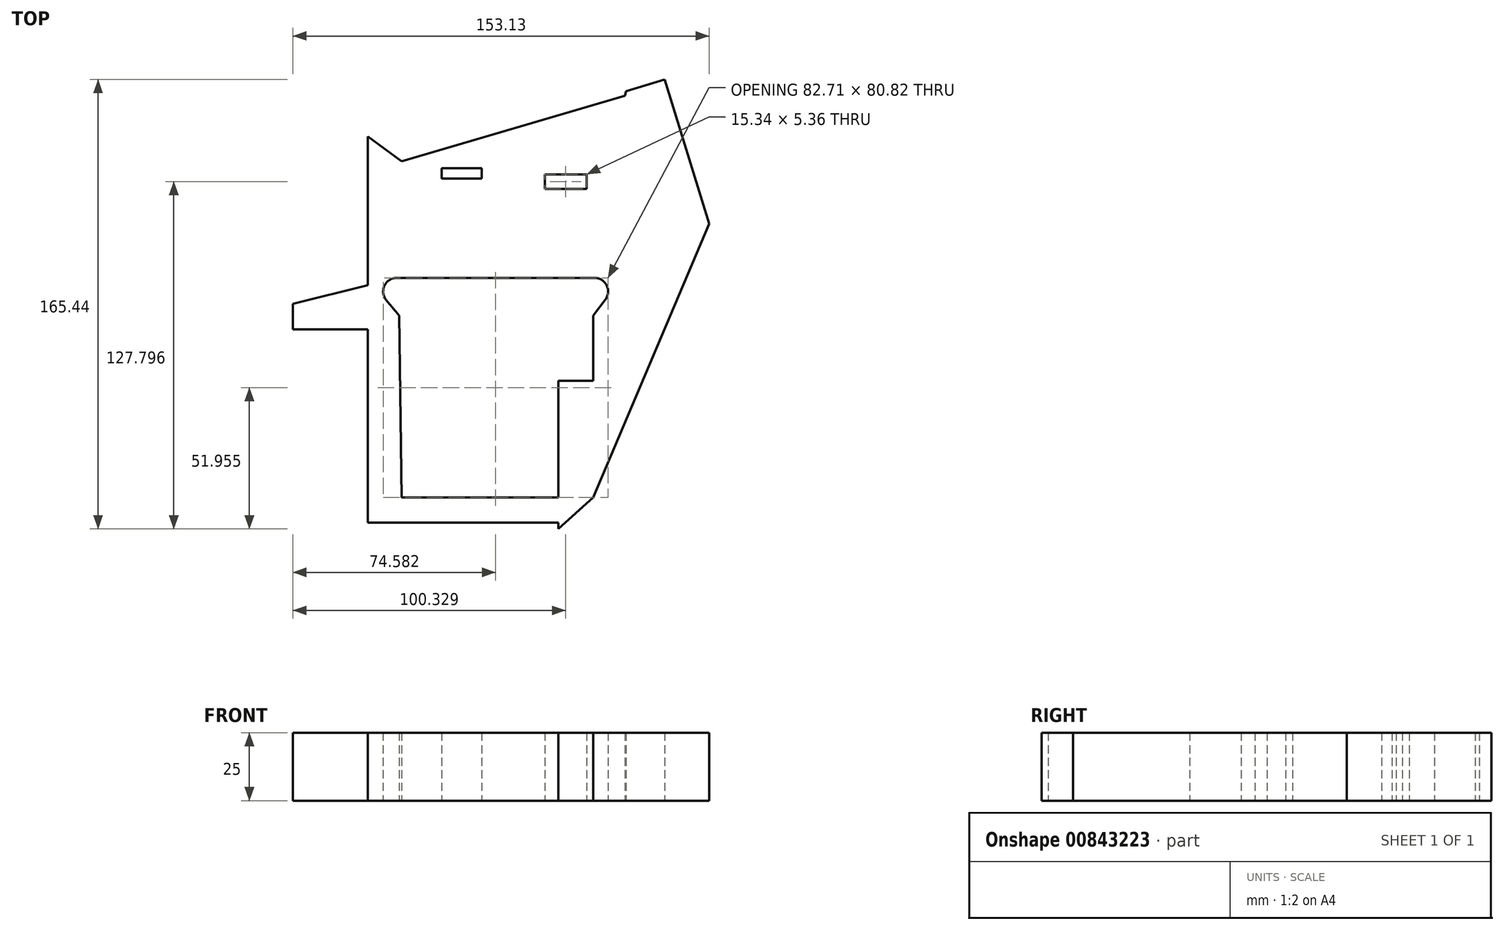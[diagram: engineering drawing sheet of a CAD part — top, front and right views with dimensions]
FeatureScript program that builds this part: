
annotation { "Feature Type Name" : "Feature", "Feature Type Description" : "" }
export const myFeature = defineFeature(function(context is Context, id is Id, definition is map)
    precondition{}
    {
        {
            var Q0;
            Q0=qCreatedBy(makeId("Top.planeOp"),FACE);
            var sketch = newSketch(context, id + "F0", { "sketchPlane" : qUnion([Q0])});
            skLineSegment(sketch, "E0", {"start": v(-30.35, 30.64) * mm, "end": v(41, 30.64) * mm});
            skLineSegment(sketch, "E1", {"start": v(41, 30.64) * mm, "end": v(41, -36.27) * mm});
            skLineSegment(sketch, "E2", {"start": v(41, -36.27) * mm, "end": v(-29.46, -36.27) * mm});
            skLineSegment(sketch, "E3", {"start": v(-29.46, -36.27) * mm, "end": v(-30.35, 30.64) * mm});
            skLineSegment(sketch, "E4", {"start": v(-30.35, 30.64) * mm, "end": v(-35.1, 36.36) * mm});
            skLineSegment(sketch, "E5", {"start": v(-31.25, 44.56) * mm, "end": v(41.53, 44.56) * mm});
            skLineSegment(sketch, "E6", {"start": v(45.5, 36.52) * mm, "end": v(41, 30.64) * mm});
            skPoint(sketch, "E7.visualSharp", {"position": v(-41.9, 44.56) * mm});
            skArc(sketch, "E7.filletArc", {"start": v(-31.25, 44.56) * mm, "mid": v(-35.77, 41.68) * mm, "end": v(-35.1, 36.36) * mm});
            skPoint(sketch, "E8.visualSharp", {"position": v(51.66, 44.56) * mm});
            skArc(sketch, "E8.filletArc", {"start": v(45.5, 36.52) * mm, "mid": v(46.02, 41.77) * mm, "end": v(41.53, 44.56) * mm});
            skLineSegment(sketch, "E9", {"start": v(-30.35, 30.64) * mm, "end": v(-41.9, 25.6) * mm});
            skLineSegment(sketch, "E10", {"start": v(-41.9, 25.6) * mm, "end": v(-41.9, -45.44) * mm});
            skLineSegment(sketch, "E11", {"start": v(-41.9, -45.44) * mm, "end": v(-29.46, -36.27) * mm});
            skLineSegment(sketch, "E12", {"start": v(41, 30.64) * mm, "end": v(28.27, 25.6) * mm});
            skLineSegment(sketch, "E13", {"start": v(28.27, 25.6) * mm, "end": v(28.27, -47.81) * mm});
            skLineSegment(sketch, "E14", {"start": v(28.27, -47.81) * mm, "end": v(41, -36.27) * mm});
            skLineSegment(sketch, "E15", {"start": v(-41.9, -45.44) * mm, "end": v(28.27, -45.44) * mm});
            skLineSegment(sketch, "E16", {"start": v(-41.9, 25.6) * mm, "end": v(28.27, 25.6) * mm});
            skLineSegment(sketch, "E17.bottom", {"start": v(5.18, -6.07) * mm, "end": v(23.24, -6.07) * mm});
            skLineSegment(sketch, "E17.top", {"start": v(5.18, -13.47) * mm, "end": v(23.24, -13.47) * mm});
            skLineSegment(sketch, "E17.left", {"start": v(5.18, -6.07) * mm, "end": v(5.18, -13.47) * mm});
            skLineSegment(sketch, "E17.right", {"start": v(23.24, -6.07) * mm, "end": v(23.24, -13.47) * mm});
            skLineSegment(sketch, "E18.bottom", {"start": v(-22.65, -6.07) * mm, "end": v(-6.96, -6.07) * mm});
            skLineSegment(sketch, "E18.top", {"start": v(-22.65, -13.47) * mm, "end": v(-6.96, -13.47) * mm});
            skLineSegment(sketch, "E18.left", {"start": v(-22.65, -6.07) * mm, "end": v(-22.65, -13.47) * mm});
            skLineSegment(sketch, "E18.right", {"start": v(-6.96, -6.07) * mm, "end": v(-6.96, -13.47) * mm});
            skLineSegment(sketch, "E19", {"start": v(-17.91, -13.47) * mm, "end": v(-17.91, -6.07) * mm});
            skLineSegment(sketch, "E20", {"start": v(-11.7, -13.47) * mm, "end": v(-11.7, -6.07) * mm});
            skLineSegment(sketch, "E21", {"start": v(11.4, -13.47) * mm, "end": v(11.4, -6.07) * mm});
            skLineSegment(sketch, "E22", {"start": v(17.02, -13.47) * mm, "end": v(17.02, -6.07) * mm});
            skLineSegment(sketch, "E23", {"start": v(-6.07, 3.7) * mm, "end": v(-5.59, -32.43) * mm});
            skLineSegment(sketch, "E24", {"start": v(-5.59, -32.43) * mm, "end": v(3.1, -32.32) * mm});
            skLineSegment(sketch, "E25", {"start": v(3.1, -32.32) * mm, "end": v(3.1, 3.7) * mm});
            skLineSegment(sketch, "E26", {"start": v(3.1, 3.7) * mm, "end": v(-6.07, 3.7) * mm});
            skLineSegment(sketch, "E27", {"start": v(8.44, 15.84) * mm, "end": v(23.24, 15.84) * mm});
            skLineSegment(sketch, "E28", {"start": v(23.24, 15.84) * mm, "end": v(23.24, 7.55) * mm});
            skLineSegment(sketch, "E29", {"start": v(23.24, 7.55) * mm, "end": v(9.62, 7.55) * mm});
            skLineSegment(sketch, "E30", {"start": v(9.62, 7.55) * mm, "end": v(9.62, 15.84) * mm});
            skLineSegment(sketch, "E31.bottom", {"start": v(-22.35, 17.02) * mm, "end": v(-8.44, 17.02) * mm});
            skLineSegment(sketch, "E31.top", {"start": v(-22.35, 9.03) * mm, "end": v(-8.44, 9.03) * mm});
            skLineSegment(sketch, "E31.left", {"start": v(-22.35, 17.02) * mm, "end": v(-22.35, 9.03) * mm});
            skLineSegment(sketch, "E31.right", {"start": v(-8.44, 17.02) * mm, "end": v(-8.44, 9.03) * mm});
            skLineSegment(sketch, "E32", {"start": v(-31.25, 44.56) * mm, "end": v(-69.43, 35.08) * mm});
            skLineSegment(sketch, "E33", {"start": v(-69.43, 35.08) * mm, "end": v(-69.43, 25.6) * mm});
            skLineSegment(sketch, "E34", {"start": v(-69.43, 25.6) * mm, "end": v(-41.9, 25.6) * mm});
            skLineSegment(sketch, "E35", {"start": v(41.53, 44.56) * mm, "end": v(0, 26.45) * mm});
            skLineSegment(sketch, "E36.MirrorCS", {"start": v(-31.25, 6.66) * mm, "end": v(41.53, 6.66) * mm});
            skLineSegment(sketch, "E37.MirrorCS", {"start": v(-29.46, 87.48) * mm, "end": v(-30.35, 20.58) * mm});
            skLineSegment(sketch, "E38.MirrorCS", {"start": v(-41.9, 25.6) * mm, "end": v(-41.9, 96.66) * mm});
            skLineSegment(sketch, "E39", {"start": v(41, -36.27) * mm, "end": v(83.7, 64.5) * mm});
            skLineSegment(sketch, "E40", {"start": v(83.7, 64.5) * mm, "end": v(67.34, 117.63) * mm});
            skLineSegment(sketch, "E41", {"start": v(67.34, 117.63) * mm, "end": v(53.08, 113.24) * mm});
            skLineSegment(sketch, "E42", {"start": v(53.08, 113.24) * mm, "end": v(40, 43.9) * mm});
            skLineSegment(sketch, "E43", {"start": v(40, 43.9) * mm, "end": v(-29.46, 87.48) * mm});
            skLineSegment(sketch, "E44", {"start": v(52.78, 111.64) * mm, "end": v(-29.46, 87.48) * mm});
            skLineSegment(sketch, "E45", {"start": v(-41.9, 96.66) * mm, "end": v(-29.46, 87.48) * mm});
            skLineSegment(sketch, "E46.bottom", {"start": v(38.57, 77.3) * mm, "end": v(23.23, 77.3) * mm});
            skLineSegment(sketch, "E46.top", {"start": v(38.57, 82.67) * mm, "end": v(23.23, 82.67) * mm});
            skLineSegment(sketch, "E46.left", {"start": v(38.57, 77.3) * mm, "end": v(38.57, 82.67) * mm});
            skLineSegment(sketch, "E46.right", {"start": v(23.23, 77.3) * mm, "end": v(23.23, 82.67) * mm});
            skLineSegment(sketch, "E47.bottom", {"start": v(0, 84.95) * mm, "end": v(-14.76, 84.95) * mm});
            skLineSegment(sketch, "E47.top", {"start": v(0, 81.07) * mm, "end": v(-14.76, 81.07) * mm});
            skLineSegment(sketch, "E47.left", {"start": v(0, 84.95) * mm, "end": v(0, 81.07) * mm});
            skLineSegment(sketch, "E47.right", {"start": v(-14.76, 84.95) * mm, "end": v(-14.76, 81.07) * mm});
            skSolve(sketch);
        }
        {
            var Q0;
            Q0 = qSketchRegion(id + "F0", true);
            extrude(context, id + "F1", {"entities" : qUnion([Q0]), "depth" : 25 * mm, "offsetDistance" : 25 * mm});
        }
    });
